# Revit family: Indirect-Water-Heater_AO_Smith-IT-400_N_B
name_source: partatom
category: Mechanical Equipment
revit_build: Autodesk Revit 2016 (Build: 20170117_1200(x64)
units: mm (PartAtom-declared; Revit-internal decimal feet)

## family parameters
Always vertical = Yes
Cut with Voids When Loaded = No
OmniClass Number = 23.75.00.00
OmniClass Title = Climate Control (HVAC)
Part Type = Normal
Room Calculation Point = No
Round Connector Dimension = Use Radius
Shared = No
Work Plane-Based = No

## types (1)
- IT 400 N B
    1e Maintenance (check-up) = 3 maanden na installatie
    2nd Maintenance (general maintenance) = 12 maanden na installatie
    Assembly Code = D3010
    BIM Content Developer = CAD & Company
    BIM Content Developer URL = http://www.cadcompany.nl
    Category = Mechanical Equipment
    Cold Water Connection R = 2"
    Description = Indirecte Boiler met 1 warmtewisselaar
    Destination / Counrty = Nederland
    Diameter (with insulation) = 740 mm  [stored 2.42782 ft]
    Diameter (without insulation) = 600 mm  [stored 1.9685 ft]
    Draw-off Capacity @ ΔT = 28°C after 120 min. = 5442.0 L
    Draw-off Capacity @ ΔT = 28°C after 30 min. = 1848.0 L
    Draw-off Capacity @ ΔT = 28°C after 60 min. = 3046.0 L
    Draw-off Capacity @ ΔT = 28°C after 90 min. = 4244.0 L
    Draw-off Capacity @ ΔT = 44°C after 120 min. = 3463.0 L
    Draw-off Capacity @ ΔT = 44°C after 30 min. = 1176.0 L
    Draw-off Capacity @ ΔT = 44°C after 60 min. = 1938.0 L
    Draw-off Capacity @ ΔT = 44°C after 90 min. = 2701.0 L
    Draw-off Capacity @ ΔT = 50°C after 120 min. = 3047.0 L
    Draw-off Capacity @ ΔT = 50°C after 30 min. = 1035.0 L
    Draw-off Capacity @ ΔT = 50°C after 60 min. = 1706.0 L
    Draw-off Capacity @ ΔT = 50°C after 90 min. = 2377.0 L
    Draw-off Capacity @ ΔT = 55°C after 120 min. = 2770.0 L
    Draw-off Capacity @ ΔT = 55°C after 30 min. = 941.0 L
    Draw-off Capacity @ ΔT = 55°C after 60 min. = 1551.0 L
    Draw-off Capacity @ ΔT = 55°C after 90 min. = 2160.0 L
    Draw-off Capacity @ ΔT = 70°C after 120 min. = 2177.0 L
    Draw-off Capacity @ ΔT = 70°C after 30 min. = 739.0 L
    Draw-off Capacity @ ΔT = 70°C after 60 min. = 1218.0 L
    Draw-off Capacity @ ΔT = 70°C after 90 min. = 1698.0 L
    Empty Weight = 139.00 kg
    Flow Rate - Volume L/h = 3354
    Heating Up Time @ ΔT = 28°C = 10
    Heating Up Time @ ΔT = 44°C = 15
    Heating Up Time @ ΔT = 50°C = 17
    Heating Up Time @ ΔT = 55°C = 19
    Heating Up Time @ ΔT = 70°C = 24
    Height (with insulation) = 1710 mm  [stored 5.61024 ft]
    Height (without insulation) = 1655 mm  [stored 5.42979 ft]
    Height Cold Water Inlet = 70 mm  [stored 0.229659 ft]
    Height Warm Water Outlet = 1655 mm  [stored 5.42979 ft]
    Host = Unhosted
    Hot / Warm Water Connection R = 2"
    Insulation Thickness = 70 mm  [stored 0.229659 ft]
    Maintenance Interval = 12 maanden
    Manufacturer = A.O. Smith Water Products Company b.v.
    Manufacturer Number = E 7110
E 7110
E 7110
    Max. Operating Pressure - bottom heat exchanger = 1600000.0 Pa
    Max. Operating Pressure - tank = 1000000.0 Pa
    Max. Tempature - bottom heat exchanger = 110 °C
    Max. Temperature - tank = 95 °C
    Model = IT 400 N B
    NLSfB = 51.11
    Nominal Output - bottom heat exchanger = 78000 W
    Operating Weight = 524.00 kg
    Packaging Height = 1850 mm  [stored 6.06955 ft]
    Packaging Length = 780 mm  [stored 2.55906 ft]
    Packaging Width = 780 mm  [stored 2.55906 ft]
    Pressure Loss - bottom heat exchanger 80ºC/60ºC = 24400.0 Pa
    Product Documentation Link = https://www.aosmithinternational.com
    Product Instruction Link = https://www.aosmithinternational.com
    Productcode = 8717449181406
    Productversion = 1.0
    Recovery Rate @ ΔT = 28°C (ltr/hr) = 2396
    Recovery Rate @ ΔT = 44°C (ltr/hr) = 1525
    Recovery Rate @ ΔT = 50°C (ltr/hr) = 1342
    Recovery Rate @ ΔT = 55°C (ltr/hr) = 1220
    Recovery Rate @ ΔT = 70°C (ltr/hr) = 958
    Serial Number = 8717449181406
    Stand-by Loss = 0 W
    Stand-by Loss - daily (Watt/24H) = 0
    Storage Capacity - bottom heat exchanger = 14.8 m³
    Storage Capacity - tank = 385 m³
    Surface bottom heat Exchanger = 2.45 m²
    T&P Connection Rp = 1"
    Transport Weight = 153.00 kg
    Type of Packaging = Plastic en Hout
    URL = www.aosmith.nl
    Warranty on Parts = 12 maanden
    Warranty on Tank = 36 maanden
    Workspace Diameter = 1740 mm
    Workspace Height = 2710 mm  [stored 8.89108 ft]

note: [stored X ft] marks values corroborated as IEEE doubles in the binary element streams (Revit-internal decimal feet)

## geometry (parser evidence)
native form markers: Blend x2, Sweep x20
no freeform markers — native parametric forms only
